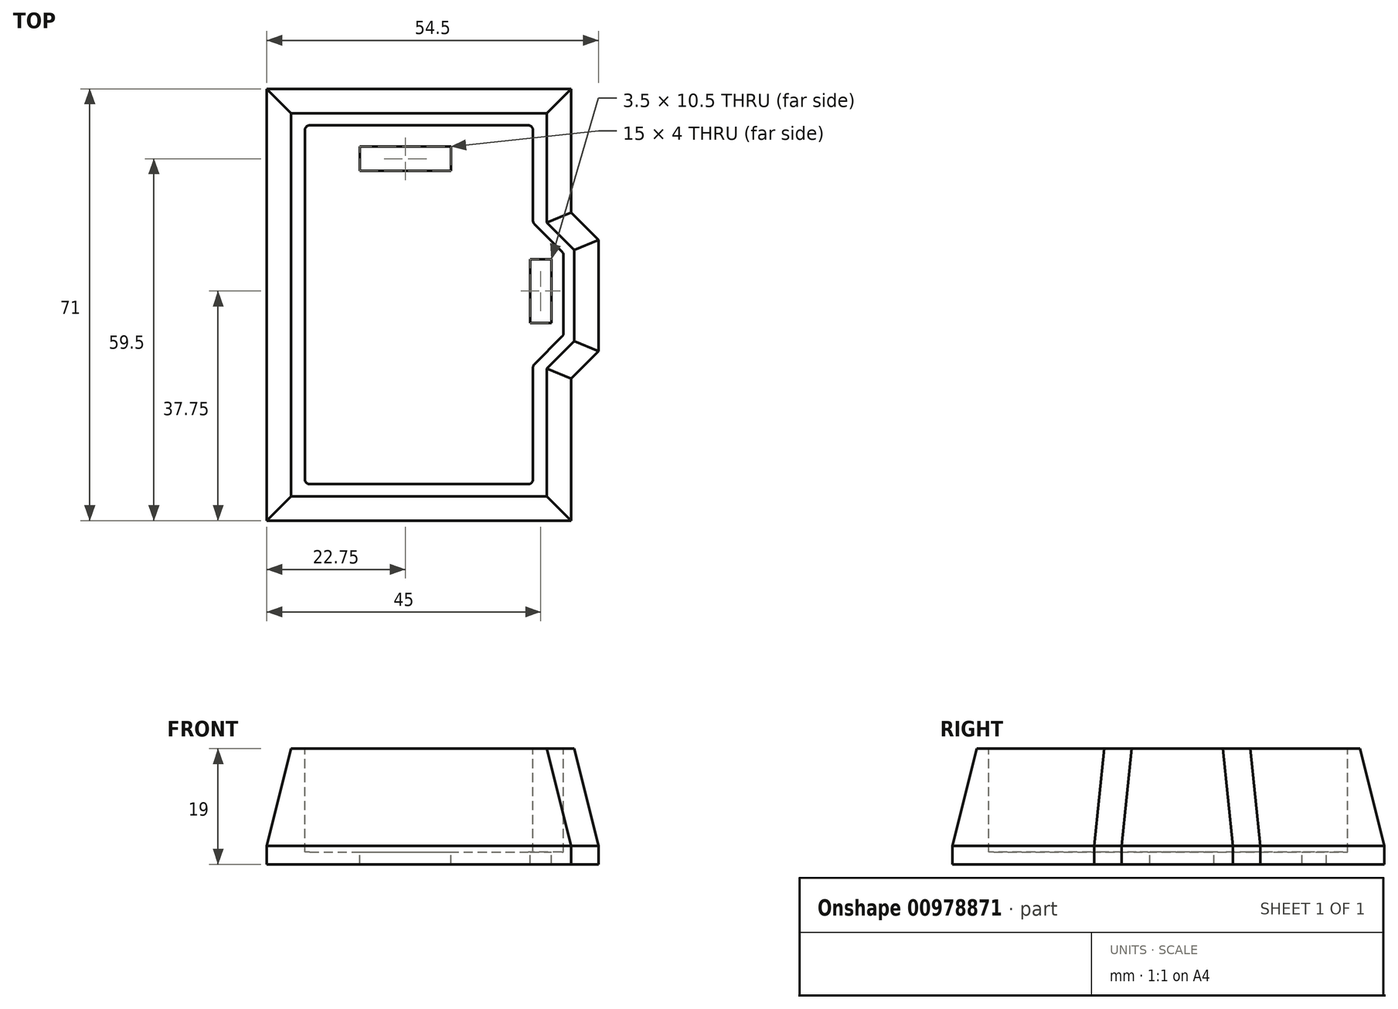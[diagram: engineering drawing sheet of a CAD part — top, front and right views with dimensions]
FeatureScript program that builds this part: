
annotation { "Feature Type Name" : "Feature", "Feature Type Description" : "" }
export const myFeature = defineFeature(function(context is Context, id is Id, definition is map)
    precondition{}
    {
        {
            var Q0;
            Q0=qCreatedBy(makeId("Top.planeOp"),FACE);
            var sketch = newSketch(context, id + "F0", { "sketchPlane" : qUnion([Q0])});
            skLineSegment(sketch, "E0.0", {"start": v(-4, -4) * mm, "end": v(46, -4) * mm});
            skLineSegment(sketch, "E0.1", {"start": v(46, -4) * mm, "end": v(46, 19.34) * mm});
            skLineSegment(sketch, "E0.2", {"start": v(-4, -4) * mm, "end": v(-4, 67) * mm});
            skLineSegment(sketch, "E0.3", {"start": v(50.5, 23.84) * mm, "end": v(46, 19.34) * mm});
            skLineSegment(sketch, "E0.4", {"start": v(-4, 67) * mm, "end": v(46, 67) * mm});
            skLineSegment(sketch, "E0.5", {"start": v(46, 46.66) * mm, "end": v(46, 67) * mm});
            skLineSegment(sketch, "E0.6", {"start": v(46, 46.66) * mm, "end": v(50.5, 42.16) * mm});
            skLineSegment(sketch, "E0.7", {"start": v(50.5, 42.16) * mm, "end": v(50.5, 23.84) * mm});
            skSolve(sketch);
        }
        {
            var Q0;
            Q0=qCreatedBy(makeId("Top.planeOp"),FACE);
            cPlane(context, id + "F1", {"entities" : qUnion([Q0]), "cplaneType" : CPlaneType.OFFSET, "offset" : 16 * mm, "width" : 150 * mm, "height" : 150 * mm});
        }
        {
            var Q0;
            Q0=qCreatedBy(id+"F1.planeOp",FACE);
            var sketch = newSketch(context, id + "F2", { "sketchPlane" : qUnion([Q0])});
            skLineSegment(sketch, "E1.bottom", {"start": v(0, 0) * mm, "end": v(42, 0) * mm});
            skLineSegment(sketch, "E1.top", {"start": v(0, 63) * mm, "end": v(42, 63) * mm});
            skLineSegment(sketch, "E1.left", {"start": v(0, 0) * mm, "end": v(0, 63) * mm});
            skLineSegment(sketch, "E1.right", {"start": v(42, 0) * mm, "end": v(42, 21) * mm});
            skLineSegment(sketch, "E2", {"start": v(42, 45) * mm, "end": v(46.5, 40.5) * mm});
            skLineSegment(sketch, "E3", {"start": v(46.5, 40.5) * mm, "end": v(46.5, 25.5) * mm});
            skLineSegment(sketch, "E4", {"start": v(46.5, 25.5) * mm, "end": v(42, 21) * mm});
            skLineSegment(sketch, "E5.trimOffspring", {"start": v(42, 45) * mm, "end": v(42, 63) * mm});
            skSolve(sketch);
        }
        {
            var Q0;
            Q0=makeQuery(id+"F0.imprint","IMPRINT",FACE,{"disambiguationData":[TD([[makeQuery(id+"F0.imprint","IMPRINT",EDGE,{"derivedFrom":sQuery(id+"F0.wireOp",EDGE,"E0.0")}),1.0]])]});
            var Q1;
            Q1=makeQuery(id+"F2.imprint","IMPRINT",FACE,{"disambiguationData":[TD([[makeQuery(id+"F2.imprint","IMPRINT",EDGE,{"derivedFrom":sQuery(id+"F2.wireOp",EDGE,"E1.bottom")}),1.0]])]});
            loft(context, id + "F3", {"sheetProfilesArray" : [{ "sheetProfileEntities" : qUnion([Q0]) }, { "sheetProfileEntities" : qUnion([Q1]) }]});
        }
        {
            var Q0;
            Q0=makeQuery(id+"F3.opLoft","CAP_FACE",FACE,{"disambiguationData":[OSD([makeQuery(id+"F0.imprint","IMPRINT",FACE,{"disambiguationData":[TD([[makeQuery(id+"F0.imprint","IMPRINT",EDGE,{"derivedFrom":sQuery(id+"F0.wireOp",EDGE,"E0.0")}),1.0]])]})])],"isStart":true});
            var sketch = newSketch(context, id + "F4", { "sketchPlane" : qUnion([Q0])});
            skSolve(sketch);
        }
        {
            var Q0;
            {var subQ2=sQuery(id+"F0.wireOp",EDGE,"E0.1");var subQ3=sQuery(id+"F0.wireOp",EDGE,"E0.0");var subQ5=sQuery(id+"F0.wireOp",EDGE,"E0.2");Q0=makeQuery(id+"F4.imprint","IMPRINT",FACE,{"disambiguationData":[TD([[makeQuery(id+"F4.imprint","IMPRINT",EDGE,{"derivedFrom":makeQuery(id+"F3.opLoft","MID_CAP_EDGE",EDGE,{"disambiguationData":[OSD([subQ3,subQ2,subQ5])],"capPos":0.0})}),-1.0]])]});}
            extrude(context, id + "F5", {"entities" : qUnion([Q0]), "operationType" : NewBodyOperationType.ADD, "depth" : 3 * mm, "offsetDistance" : 25 * mm});
        }
        {
            var Q0;
            Q0=makeQuery(id+"F3.opLoft","CAP_FACE",FACE,{"disambiguationData":[OSD([makeQuery(id+"F2.imprint","IMPRINT",FACE,{"disambiguationData":[TD([[makeQuery(id+"F2.imprint","IMPRINT",EDGE,{"derivedFrom":sQuery(id+"F2.wireOp",EDGE,"E1.bottom")}),1.0]])]})])],"isStart":true});
            var sketch = newSketch(context, id + "F6", { "sketchPlane" : qUnion([Q0])});
            skLineSegment(sketch, "E6", {"start": v(21, 63) * mm, "end": v(21, 0) * mm, "construction": true});
            skLineSegment(sketch, "E7", {"start": v(3.05, 61) * mm, "end": v(38.95, 61) * mm});
            skLineSegment(sketch, "E8", {"start": v(39.75, 60.2) * mm, "end": v(39.75, 45.33) * mm});
            skLineSegment(sketch, "E9", {"start": v(39.98, 44.77) * mm, "end": v(44.52, 40.23) * mm});
            skLineSegment(sketch, "E10", {"start": v(44.75, 39.67) * mm, "end": v(44.75, 26.83) * mm});
            skLineSegment(sketch, "E11", {"start": v(44.52, 26.27) * mm, "end": v(39.98, 21.73) * mm});
            skLineSegment(sketch, "E12", {"start": v(39.75, 21.17) * mm, "end": v(39.75, 2.8) * mm});
            skLineSegment(sketch, "E13", {"start": v(38.95, 2) * mm, "end": v(3.05, 2) * mm});
            skLineSegment(sketch, "E14", {"start": v(2.25, 2.8) * mm, "end": v(2.25, 60.2) * mm});
            skPoint(sketch, "E15", {"position": v(21, 61) * mm});
            skLineSegment(sketch, "E16", {"start": v(0, 31.5) * mm, "end": v(44.75, 31.5) * mm, "construction": true});
            skPoint(sketch, "E17", {"position": v(2.25, 31.5) * mm});
            skPoint(sketch, "E18.visualSharp", {"position": v(2.25, 61) * mm});
            skArc(sketch, "E18.filletArc", {"start": v(3.05, 61) * mm, "mid": v(2.48, 60.77) * mm, "end": v(2.25, 60.2) * mm});
            skPoint(sketch, "E19.visualSharp", {"position": v(2.25, 2) * mm});
            skArc(sketch, "E19.filletArc", {"start": v(2.25, 2.8) * mm, "mid": v(2.48, 2.23) * mm, "end": v(3.05, 2) * mm});
            skPoint(sketch, "E20.visualSharp", {"position": v(39.75, 2) * mm});
            skArc(sketch, "E20.filletArc", {"start": v(38.95, 2) * mm, "mid": v(39.52, 2.23) * mm, "end": v(39.75, 2.8) * mm});
            skPoint(sketch, "E21.visualSharp", {"position": v(39.75, 61) * mm});
            skArc(sketch, "E21.filletArc", {"start": v(39.75, 60.2) * mm, "mid": v(39.52, 60.77) * mm, "end": v(38.95, 61) * mm});
            skPoint(sketch, "E22.visualSharp", {"position": v(39.75, 45) * mm});
            skArc(sketch, "E22.filletArc", {"start": v(39.75, 45.33) * mm, "mid": v(39.81, 45.03) * mm, "end": v(39.98, 44.77) * mm});
            skPoint(sketch, "E23.visualSharp", {"position": v(44.75, 40) * mm});
            skArc(sketch, "E23.filletArc", {"start": v(44.75, 39.67) * mm, "mid": v(44.69, 39.97) * mm, "end": v(44.52, 40.23) * mm});
            skPoint(sketch, "E24.visualSharp", {"position": v(44.75, 26.5) * mm});
            skArc(sketch, "E24.filletArc", {"start": v(44.52, 26.27) * mm, "mid": v(44.69, 26.53) * mm, "end": v(44.75, 26.83) * mm});
            skPoint(sketch, "E25.visualSharp", {"position": v(39.75, 21.5) * mm});
            skArc(sketch, "E25.filletArc", {"start": v(39.98, 21.73) * mm, "mid": v(39.81, 21.47) * mm, "end": v(39.75, 21.17) * mm});
            skSolve(sketch);
        }
        {
            var Q0;
            Q0 = qSketchRegion(id + "F6", true);
            extrude(context, id + "F7", {"entities" : qUnion([Q0]), "operationType" : NewBodyOperationType.REMOVE, "oppositeDirection" : true, "depth" : 17 * mm, "offsetDistance" : 25 * mm});
        }
        {
            var Q0;
            Q0=makeQuery(id+"F7.boolean.opBoolean","COPY",FACE,{"derivedFrom":makeQuery(id+"F7.opExtrude","CAP_FACE",FACE,{"disambiguationData":[OSD([sQuery(id+"F6.wireOp",EDGE,"E7"),sQuery(id+"F6.wireOp",EDGE,"E8"),sQuery(id+"F6.wireOp",EDGE,"E9"),sQuery(id+"F6.wireOp",EDGE,"E10"),sQuery(id+"F6.wireOp",EDGE,"E11"),sQuery(id+"F6.wireOp",EDGE,"E12"),sQuery(id+"F6.wireOp",EDGE,"E13"),sQuery(id+"F6.wireOp",EDGE,"E14"),sQuery(id+"F6.wireOp",EDGE,"E18.filletArc"),sQuery(id+"F6.wireOp",EDGE,"E19.filletArc"),sQuery(id+"F6.wireOp",EDGE,"E20.filletArc"),sQuery(id+"F6.wireOp",EDGE,"E21.filletArc"),sQuery(id+"F6.wireOp",EDGE,"E22.filletArc"),sQuery(id+"F6.wireOp",EDGE,"E23.filletArc"),sQuery(id+"F6.wireOp",EDGE,"E24.filletArc"),sQuery(id+"F6.wireOp",EDGE,"E25.filletArc")])],"isStart":false})});
            var sketch = newSketch(context, id + "F8", { "sketchPlane" : qUnion([Q0])});
            skLineSegment(sketch, "E26.bottom", {"start": v(11.25, 57.5) * mm, "end": v(26.25, 57.5) * mm});
            skLineSegment(sketch, "E26.top", {"start": v(11.25, 53.5) * mm, "end": v(26.25, 53.5) * mm});
            skLineSegment(sketch, "E26.left", {"start": v(11.25, 57.5) * mm, "end": v(11.25, 53.5) * mm});
            skLineSegment(sketch, "E26.right", {"start": v(26.25, 57.5) * mm, "end": v(26.25, 53.5) * mm});
            skLineSegment(sketch, "E27.bottom", {"start": v(39.25, 39) * mm, "end": v(42.75, 39) * mm});
            skLineSegment(sketch, "E27.top", {"start": v(39.25, 28.5) * mm, "end": v(42.75, 28.5) * mm});
            skLineSegment(sketch, "E27.left", {"start": v(39.25, 39) * mm, "end": v(39.25, 28.5) * mm});
            skLineSegment(sketch, "E27.right", {"start": v(42.75, 39) * mm, "end": v(42.75, 28.5) * mm});
            skSolve(sketch);
        }
        {
            var Q0;
            Q0 = qSketchRegion(id + "F8", true);
            extrude(context, id + "F9", {"entities" : qUnion([Q0]), "operationType" : NewBodyOperationType.REMOVE, "endBound" : BoundingType.THROUGH_ALL, "oppositeDirection" : true, "depth" : 25 * mm, "offsetDistance" : 25 * mm});
        }
    });
